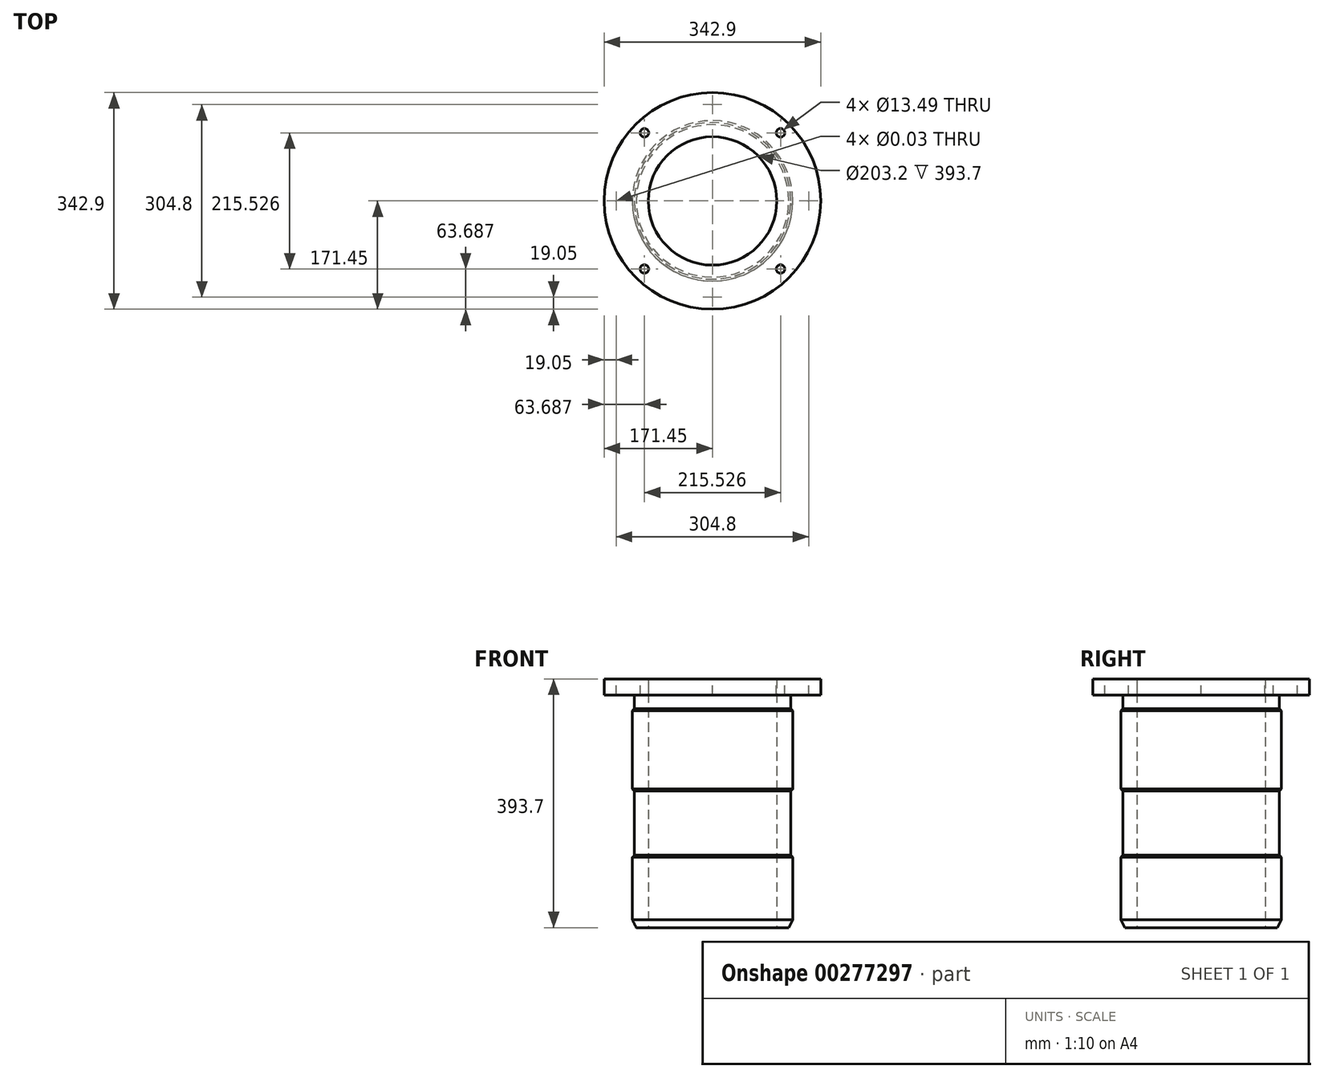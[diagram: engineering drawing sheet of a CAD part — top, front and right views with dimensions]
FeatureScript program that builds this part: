
annotation { "Feature Type Name" : "Feature", "Feature Type Description" : "" }
export const myFeature = defineFeature(function(context is Context, id is Id, definition is map)
    precondition{}
    {
        {
            var Q0;
            Q0=qCreatedBy(makeId("Top.planeOp"),FACE);
            var sketch = newSketch(context, id + "F0", { "sketchPlane" : qUnion([Q0])});
            skCircle(sketch, "E0", {"center": v(0, 0) * mm, "radius": 171.45 * mm});
            skCircle(sketch, "E1", {"center": v(0, 0) * mm, "radius": 101.6 * mm});
            skSolve(sketch);
        }
        {
            var Q0;
            Q0 = qSketchRegion(id + "F0", true);
            extrude(context, id + "F1", {"entities" : qUnion([Q0]), "depth" : 25.4 * mm});
        }
        {
            var Q0;
            Q0=makeQuery(id+"F1.opExtrude","CAP_FACE",FACE,{"disambiguationData":[OSD([sQuery(id+"F0.wireOp",EDGE,"E0"),sQuery(id+"F0.wireOp",EDGE,"E1")])],"isStart":false});
            var sketch = newSketch(context, id + "F2", { "sketchPlane" : qUnion([Q0])});
            skCircle(sketch, "E2", {"center": v(0, 0) * mm, "radius": 152.4 * mm, "construction": true});
            skLineSegment(sketch, "E3", {"start": v(0, 0) * mm, "end": v(0, 152.4) * mm, "construction": true});
            skPoint(sketch, "E4", {"position": v(0, 152.4) * mm});
            skPoint(sketch, "E5.1.0", {"position": v(-107.76, 107.76) * mm});
            skPoint(sketch, "E5.2.0", {"position": v(-152.4, 0) * mm});
            skPoint(sketch, "E5.3.0", {"position": v(-107.76, -107.76) * mm});
            skPoint(sketch, "E5.4.0", {"position": v(0, -152.4) * mm});
            skPoint(sketch, "E5.5.0", {"position": v(107.76, -107.76) * mm});
            skPoint(sketch, "E5.6.0", {"position": v(152.4, 0) * mm});
            skPoint(sketch, "E5.7.0", {"position": v(107.76, 107.76) * mm});
            skSolve(sketch);
        }
        {
            var Q0;
            Q0=sQuery(id+"F2.wireOp",VERTEX,"E5.7.0");
            var Q1;
            Q1=sQuery(id+"F2.wireOp",VERTEX,"E5.5.0");
            var Q2;
            Q2=sQuery(id+"F2.wireOp",VERTEX,"E5.3.0");
            var Q3;
            Q3=sQuery(id+"F2.wireOp",VERTEX,"E5.1.0");
            var Q4;
            Q4=makeQuery(id+"F1.opExtrude","SWEPT_BODY",BODY,{"disambiguationData":[OSD([sQuery(id+"F0.wireOp",EDGE,"E0"),sQuery(id+"F0.wireOp",EDGE,"E1")])]});
            hole(context, id + "F3", {"style" : HoleStyle.SIMPLE, "endStyle" : HoleEndStyle.THROUGH, "standardTappedOrClearance" : lookupTablePath({ "standard" : "ANSI", "engagement" : "75%", "pitch" : "11 tpi", "size" : "5/8", "type" : "Tapped" }), "standardBlindInLast" : lookupTablePath({ "standard" : "ANSI", "engagement" : "75%", "pitch" : "11 tpi", "size" : "5/8", "type" : "Tapped" }), "holeDiameter" : 13.5 * mm, "showTappedDepth" : true, "tappedDepth" : 20.63 * mm, "tapClearance" : 3, "startFromSketch" : true, "locations" : qUnion([Q0, Q1, Q2, Q3]), "scope" : qUnion([Q4]), "majorDiameter" : 15.88 * mm});
        }
        {
            var Q0;
            Q0=sQuery(id+"F2.wireOp",VERTEX,"E4");
            var Q1;
            Q1=sQuery(id+"F2.wireOp",VERTEX,"E5.2.0");
            var Q2;
            Q2=sQuery(id+"F2.wireOp",VERTEX,"E5.4.0");
            var Q3;
            Q3=sQuery(id+"F2.wireOp",VERTEX,"E5.6.0");
            var Q4;
            Q4=makeQuery(id+"F1.opExtrude","SWEPT_BODY",BODY,{"disambiguationData":[OSD([sQuery(id+"F0.wireOp",EDGE,"E0"),sQuery(id+"F0.wireOp",EDGE,"E1")])]});
            hole(context, id + "F4", {"style" : HoleStyle.SIMPLE, "endStyle" : HoleEndStyle.THROUGH, "standardTappedOrClearance" : lookupTablePath({ "standard" : "ANSI", "size" : "11/16 (0.69)", "type" : "Drilled" }), "standardBlindInLast" : lookupTablePath({ "standard" : "ANSI", "size" : "11/16", "type" : "Drilled" }), "holeDiameter" : 11 / 406.4 * mm, "tappedDepth" : 20.62 * mm, "tapClearance" : 3, "startFromSketch" : true, "locations" : qUnion([Q0, Q1, Q2, Q3]), "scope" : qUnion([Q4])});
        }
        {
            var Q0;
            Q0=makeQuery(id+"F1.opExtrude","CAP_FACE",FACE,{"disambiguationData":[OSD([sQuery(id+"F0.wireOp",EDGE,"E0"),sQuery(id+"F0.wireOp",EDGE,"E1")])],"isStart":true});
            var sketch = newSketch(context, id + "F5", { "sketchPlane" : qUnion([Q0])});
            skCircle(sketch, "E6.0", {"center": v(0, 0) * mm, "radius": 101.6 * mm});
            skCircle(sketch, "E7", {"center": v(0, 0) * mm, "radius": 127 * mm});
            skSolve(sketch);
        }
        {
            var Q0;
            Q0 = qSketchRegion(id + "F5", true);
            extrude(context, id + "F6", {"entities" : qUnion([Q0]), "operationType" : NewBodyOperationType.ADD, "depth" : 368.3 * mm});
        }
        {
            var Q0;
            Q0=makeQuery(id+"F6.opExtrude","CAP_EDGE",EDGE,{"disambiguationData":[OSD([sQuery(id+"F5.wireOp",EDGE,"E7")])],"isStart":false});
            chamfer(context, id + "F7", {"entities" : qUnion([Q0]), "chamferType" : ChamferType.TWO_OFFSETS, "width1" : 12.7 * mm, "oppositeDirection" : true, "width2" : 6.35 * mm, "tangentPropagation" : true});
        }
        {
            var Q0;
            Q0=qCreatedBy(makeId("Right.planeOp"),FACE);
            var sketch = newSketch(context, id + "F8", { "sketchPlane" : qUnion([Q0])});
            skLineSegment(sketch, "E8", {"start": v(127, 0) * mm, "end": v(127, -355.6) * mm, "construction": true});
            skLineSegment(sketch, "E9.0", {"start": v(-127, -355.6) * mm, "end": v(127, -355.6) * mm, "construction": true});
            skLineSegment(sketch, "E10", {"start": v(0, 176) * mm, "end": v(0, -508.02) * mm, "construction": true});
            skLineSegment(sketch, "E11.0", {"start": v(-127, -257.05) * mm, "end": v(127, -257.05) * mm, "construction": true});
            skLineSegment(sketch, "E12.0", {"start": v(-127, -149.1) * mm, "end": v(127, -149.1) * mm, "construction": true});
            skLineSegment(sketch, "E13.0", {"start": v(-127, -25.15) * mm, "end": v(127, -25.15) * mm, "construction": true});
            skLineSegment(sketch, "E14.bottom", {"start": v(127, -257.05) * mm, "end": v(123.83, -257.05) * mm});
            skLineSegment(sketch, "E14.top", {"start": v(127, -149.1) * mm, "end": v(123.82, -149.1) * mm});
            skLineSegment(sketch, "E14.left", {"start": v(127, -257.05) * mm, "end": v(127, -149.1) * mm});
            skLineSegment(sketch, "E14.right", {"start": v(123.83, -257.05) * mm, "end": v(123.82, -149.1) * mm});
            skLineSegment(sketch, "E15.bottom", {"start": v(127, -25.15) * mm, "end": v(123.83, -25.15) * mm});
            skLineSegment(sketch, "E15.top", {"start": v(127, -0.25) * mm, "end": v(123.83, -0.25) * mm});
            skLineSegment(sketch, "E15.left", {"start": v(127, -25.15) * mm, "end": v(127, -0.25) * mm});
            skLineSegment(sketch, "E15.right", {"start": v(123.83, -25.15) * mm, "end": v(123.83, -0.25) * mm});
            skSolve(sketch);
        }
        {
            var Q0;
            Q0 = qSketchRegion(id + "F8", true);
            var Q1;
            Q1=sQuery(id+"F8.wireOp",EDGE,"E10");
            revolve(context, id + "F9", {"operationType" : NewBodyOperationType.REMOVE, "entities" : qUnion([Q0]), "axis" : qUnion([Q1]), "revolveType" : RevolveType.FULL, "oppositeDirection" : true});
        }
        {
            var Q0;
            Q0=makeQuery(id+"F9.boolean.opBoolean","COPY",EDGE,{"derivedFrom":makeQuery(id+"F9.opRevolve","SWEPT_EDGE",EDGE,{"disambiguationData":[OSD([sQuery(id+"F8.wireOp",EDGE,"E14.top"),sQuery(id+"F8.wireOp",EDGE,"E14.right")])]})});
            var Q1;
            Q1=makeQuery(id+"F9.boolean.opBoolean","COPY",EDGE,{"derivedFrom":makeQuery(id+"F9.opRevolve","SWEPT_EDGE",EDGE,{"disambiguationData":[OSD([sQuery(id+"F8.wireOp",EDGE,"E14.bottom"),sQuery(id+"F8.wireOp",EDGE,"E14.right")])]})});
            var Q2;
            Q2=makeQuery(id+"F9.boolean.opBoolean","COPY",EDGE,{"derivedFrom":makeQuery(id+"F9.opRevolve","SWEPT_EDGE",EDGE,{"disambiguationData":[OSD([sQuery(id+"F8.wireOp",EDGE,"E15.bottom"),sQuery(id+"F8.wireOp",EDGE,"E15.right")])]})});
            chamfer(context, id + "F10", {"entities" : qUnion([Q0, Q1, Q2]), "width" : 3.17 * mm, "tangentPropagation" : true});
        }
    });
